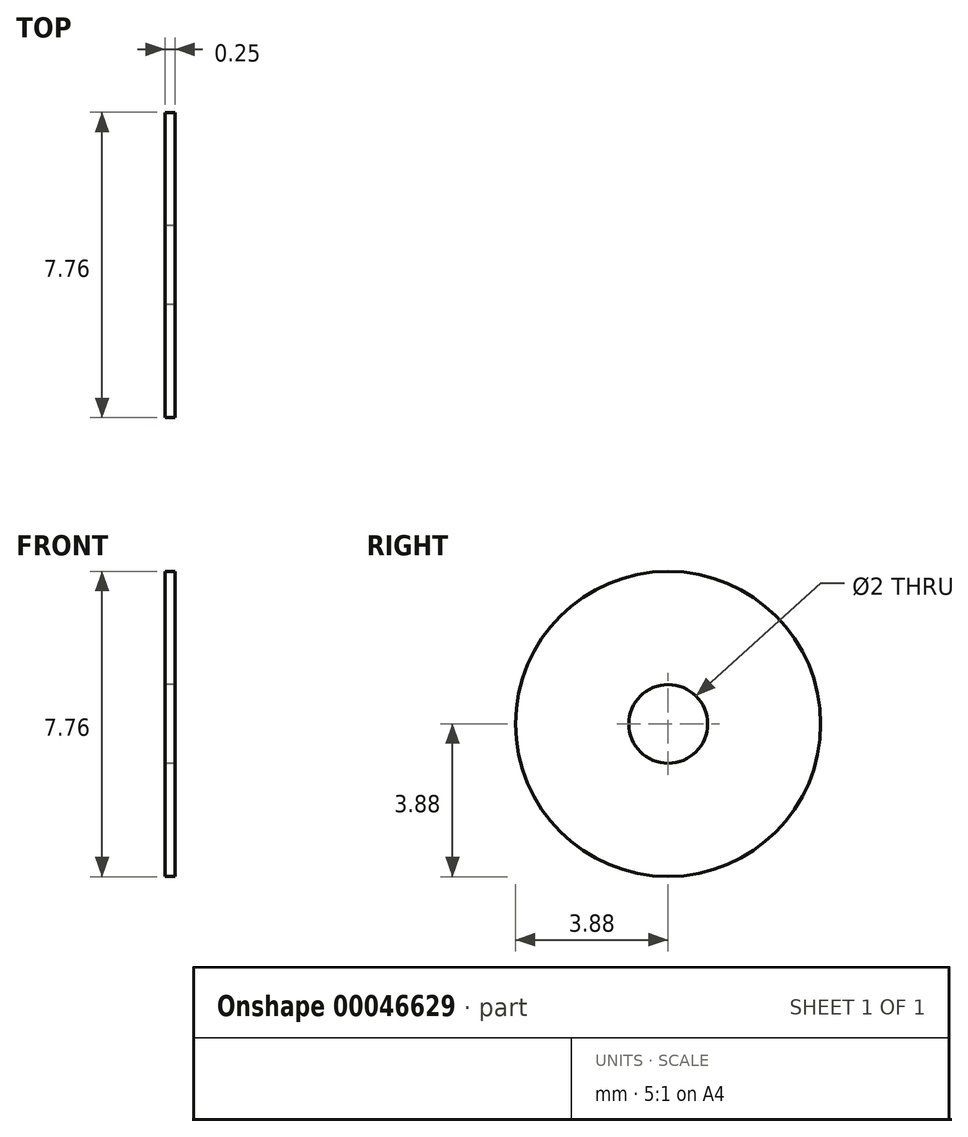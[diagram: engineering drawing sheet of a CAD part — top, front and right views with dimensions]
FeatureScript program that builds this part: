
annotation { "Feature Type Name" : "Feature", "Feature Type Description" : "" }
export const myFeature = defineFeature(function(context is Context, id is Id, definition is map)
    precondition{}
    {
        {
            var Q0;
            Q0=qCreatedBy(makeId("Right.planeOp"),FACE);
            var sketch = newSketch(context, id + "F0", { "sketchPlane" : qUnion([Q0])});
            skCircle(sketch, "E0", {"center": v(0, 0) * mm, "radius": 3.88 * mm});
            skCircle(sketch, "E1", {"center": v(0, 0) * mm, "radius": 1 * mm});
            skSolve(sketch);
        }
        {
            var Q0;
            Q0=makeQuery(id+"F0.imprint","IMPRINT",FACE,{"disambiguationData":[TD([[makeQuery(id+"F0.imprint","IMPRINT",EDGE,{"derivedFrom":sQuery(id+"F0.wireOp",EDGE,"E0")}),1.0]])]});
            extrude(context, id + "F1", {"entities" : qUnion([Q0]), "depth" : 0.25 * mm});
        }
    });
